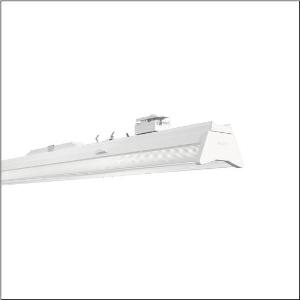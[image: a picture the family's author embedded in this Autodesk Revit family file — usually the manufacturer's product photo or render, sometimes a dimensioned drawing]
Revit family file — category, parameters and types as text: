
# Revit family: licross_r__21_performance_mo_52tm167n445g_e37c
name_source: partatom
category: Lighting Fixtures
units: mm (PartAtom-declared; Revit-internal decimal feet)

## family parameters
Cut with Voids When Loaded = No
Host = Face
Light Source = No
Part Type = Normal
Room Calculation Point = No
Round Connector Dimension = Use Diameter
Shared = No

## types (1)
- Licross® 21 Performance MO (1 x LED, 4580 lm, 24.7 W, 4000K)
    Apparent Load = 25 VA
    CIE Flux Codes = 66 88 96 79 100
    Color Rendering = 80
    Color Temperature = 4000K
    Default Elevation = 1800 mm
    Description = Licross® 21 Performance MO, luminaire insert, of sheet steel, galvanised, coil coated, white, length: 1.500mm, width: 120mm, height: 123mm, LED rated luminous flux: 4.580lm, light colour: 840, control gear: ON/OFF, with plug, 3-pole, with phase selection, mains connection: 220..240V, AC, 50/60Hz, rated input power: 25W, halogen-free wiring, primary light control with lens, of plastic, primary optical cover: cover, of PMMA, CAT 2 (L<= 3000cd/m²), light emission: direct/indirect distribution, primary light characteristic: symmetric, protection rating (complete): IP40, insulation class (complete): insulation class I (protective earthing), certification: CE, ENEC, UKCA, protection symbol: D if used in an environment without relevant dust loads with corresponding accessories, impact resistance: IK06, permissible ambient temperature for indoor applications: -35..+55°C, corresponds to IFS (International Featured Standards) requirements for safety and quality in the food industry, reducing of maximum allowable ambient temperature of 5°C with ceiling mounting, LABS conformity tested according to VDMA 24364:2018-05, packaging unit: 1 piece
    Height = 114 mm
    Lamp = 1 x LED
    Lamp Light Flux = 4580 lm
    Lamp Power = 24.7 W
    Lamp count = 1
    Length = 1500 mm
    Luminous efficacy = 185 lm/W
    Manufacturer = Siteco
    ModVariant = No
    Model = 52TM167N445G
    Mounting Place = Ceiling
    Mounting Type = Pendant
    Number of Poles = 1
    OnlyDefault = Yes
    Power Factor = 1
    Product Name = Licross® 21 Performance MO
    Product group = luminaire insert
    ProductGroupID = 901
    Protection Class = Protection class I
    Protection Degree = IP 40
    RLX_Detail_Level = 1
    RLX_Emergency_Light_Flux = 0 lm
    RLX_Emergency_Type = 0
    RLX_Emergency_Type_DB = No
    RlxData = <blob elided: 30393 chars, md5=900ec44d>
    Socket = socket
    Standby Power = 0 W
    System Light Flux = 4580 lm
    System Power = 25 W
    Type Comments = Product without accessories
    Type Image = l_1256138.jpg
    URL = http://relux.com
    VarID = ---
    Voltage = 0 V
    Weight = 0.00 kg
    Width = 120 mm

## geometry (parser evidence)
native form markers: Blend x4, Sweep x11
no freeform markers — native parametric forms only
